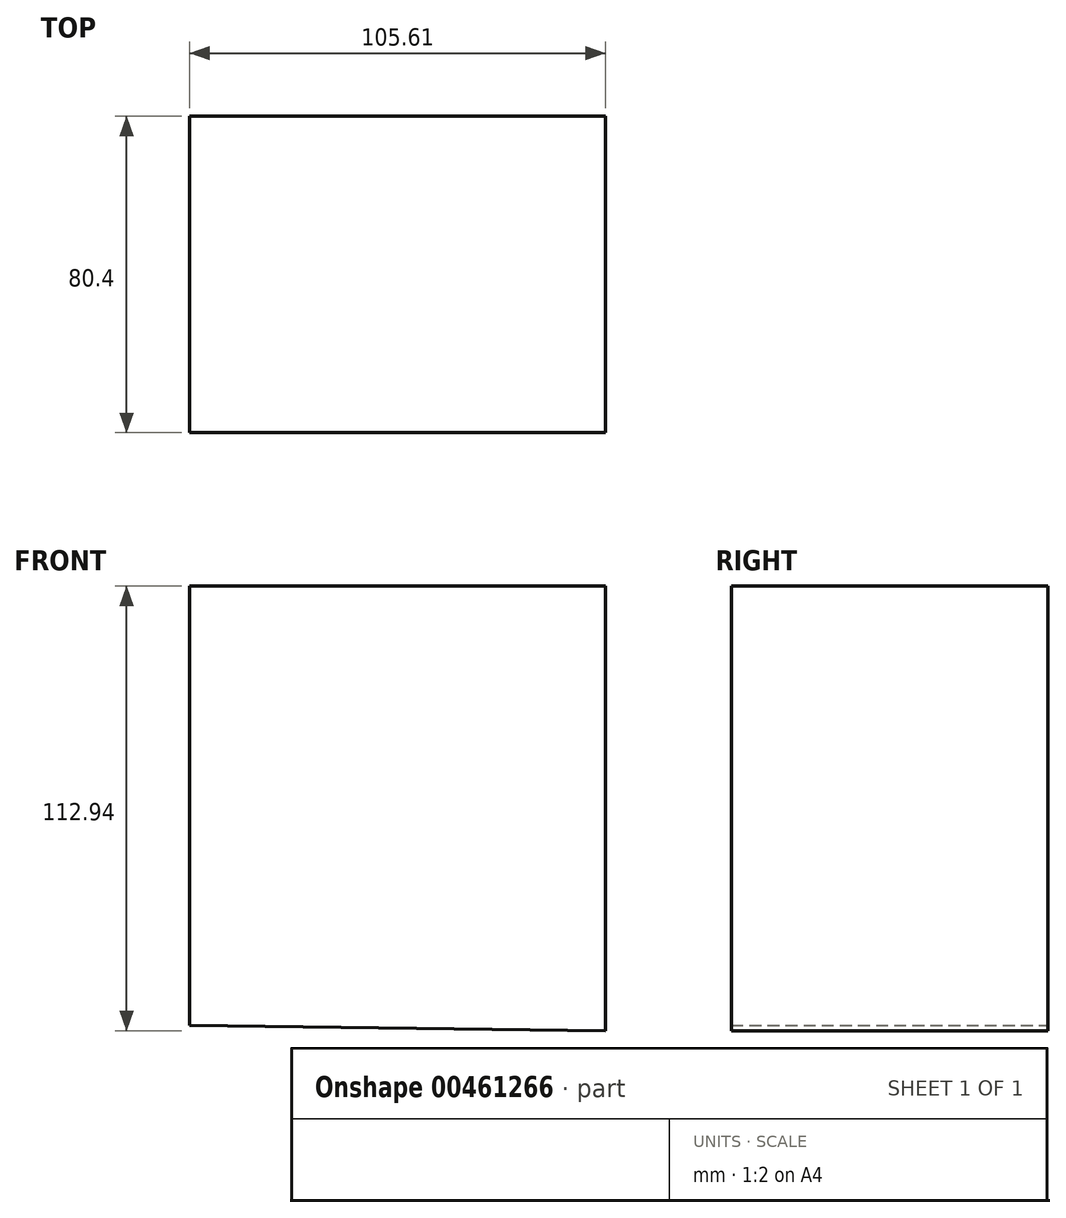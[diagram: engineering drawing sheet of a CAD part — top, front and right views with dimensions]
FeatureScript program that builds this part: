
annotation { "Feature Type Name" : "Feature", "Feature Type Description" : "" }
export const myFeature = defineFeature(function(context is Context, id is Id, definition is map)
    precondition{}
    {
        {
            var Q0;
            Q0=qCreatedBy(makeId("Front.planeOp"),FACE);
            var sketch = newSketch(context, id + "F0", { "sketchPlane" : qUnion([Q0])});
            skLineSegment(sketch, "E0", {"start": v(-46.03, -51.77) * mm, "end": v(-46.03, 59.79) * mm});
            skLineSegment(sketch, "E1", {"start": v(-46.03, 59.79) * mm, "end": v(59.58, 59.79) * mm});
            skLineSegment(sketch, "E2", {"start": v(59.58, 59.79) * mm, "end": v(59.58, -53.15) * mm});
            skLineSegment(sketch, "E3", {"start": v(59.58, -53.15) * mm, "end": v(-46.03, -51.77) * mm});
            skSolve(sketch);
        }
        {
            var Q0;
            Q0 = qSketchRegion(id + "F0", true);
            var sketch = newSketch(context, id + "F1", { "sketchPlane" : qUnion([Q0])});
            skCircle(sketch, "E4", {"center": v(61.93, 41.63) * mm, "radius": 74.62 * mm});
            skSolve(sketch);
        }
        {
            var Q0;
            Q0=makeQuery(id+"F0.imprint","IMPRINT",FACE,{"disambiguationData":[TD([[makeQuery(id+"F0.imprint","IMPRINT",EDGE,{"derivedFrom":sQuery(id+"F0.wireOp",EDGE,"E0")}),-1.0]])]});
            extrude(context, id + "F2", {"entities" : qUnion([Q0]), "depth" : 80.4 * mm});
        }
        {
            var Q0;
            Q0=sQuery(id+"F1.wireOp",EDGE,"E4");
            extrude(context, id + "F3", {"bodyType" : ToolBodyType.SURFACE, "surfaceEntities" : qUnion([Q0]), "oppositeDirection" : true, "depth" : 69.48 * mm});
        }
    });
